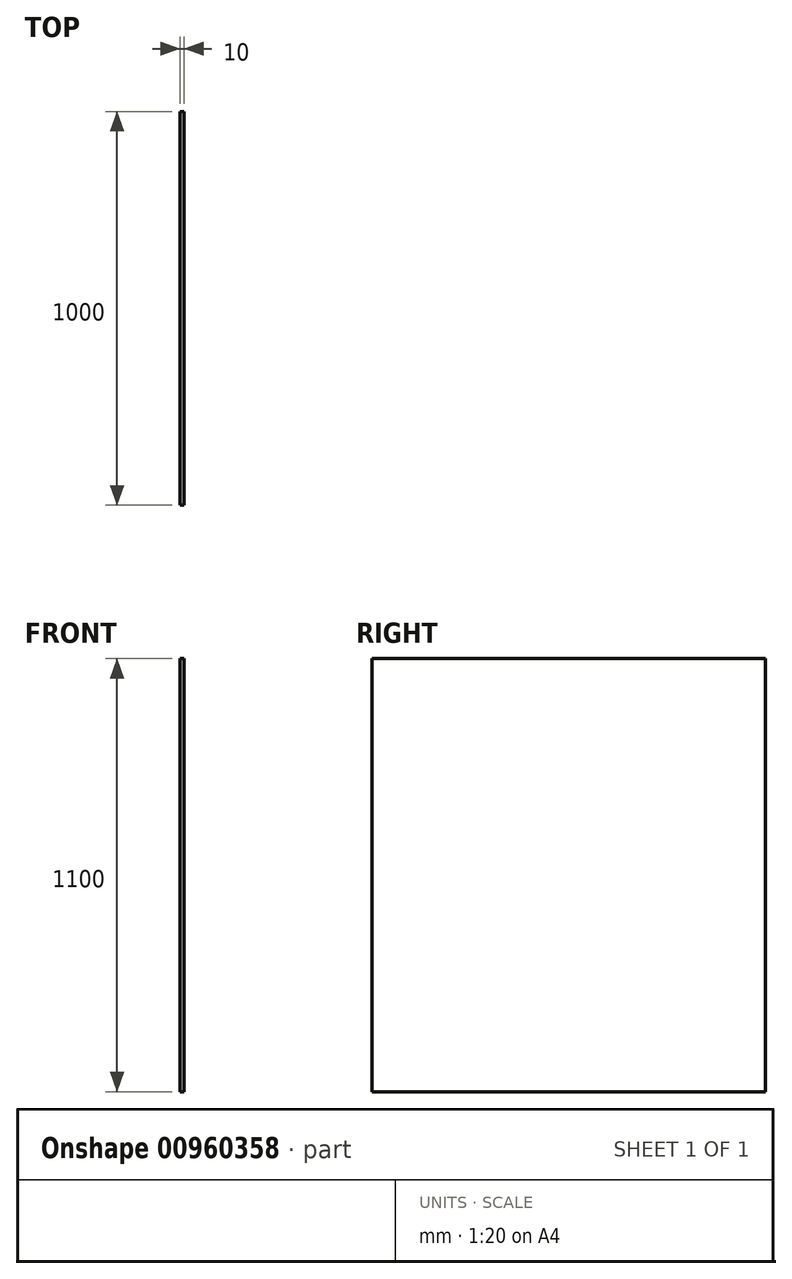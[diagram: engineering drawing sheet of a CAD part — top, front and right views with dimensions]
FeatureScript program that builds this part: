
annotation { "Feature Type Name" : "Feature", "Feature Type Description" : "" }
export const myFeature = defineFeature(function(context is Context, id is Id, definition is map)
    precondition{}
    {
        {
            var Q0;
            Q0=qCreatedBy(makeId("Right.planeOp"),FACE);
            var sketch = newSketch(context, id + "F0", { "sketchPlane" : qUnion([Q0])});
            skLineSegment(sketch, "E0.bottom", {"start": v(-500, 550) * mm, "end": v(500, 550) * mm});
            skLineSegment(sketch, "E0.top", {"start": v(-500, -550) * mm, "end": v(500, -550) * mm});
            skLineSegment(sketch, "E0.left", {"start": v(-500, 550) * mm, "end": v(-500, -550) * mm});
            skLineSegment(sketch, "E0.right", {"start": v(500, 550) * mm, "end": v(500, -550) * mm});
            skPoint(sketch, "E0.middle", {"position": v(0, 0) * mm});
            skSolve(sketch);
        }
        {
            var Q0;
            Q0 = qSketchRegion(id + "F0", true);
            extrude(context, id + "F1", {"entities" : qUnion([Q0]), "oppositeDirection" : true, "depth" : 10 * mm, "offsetDistance" : 25 * mm});
        }
    });
